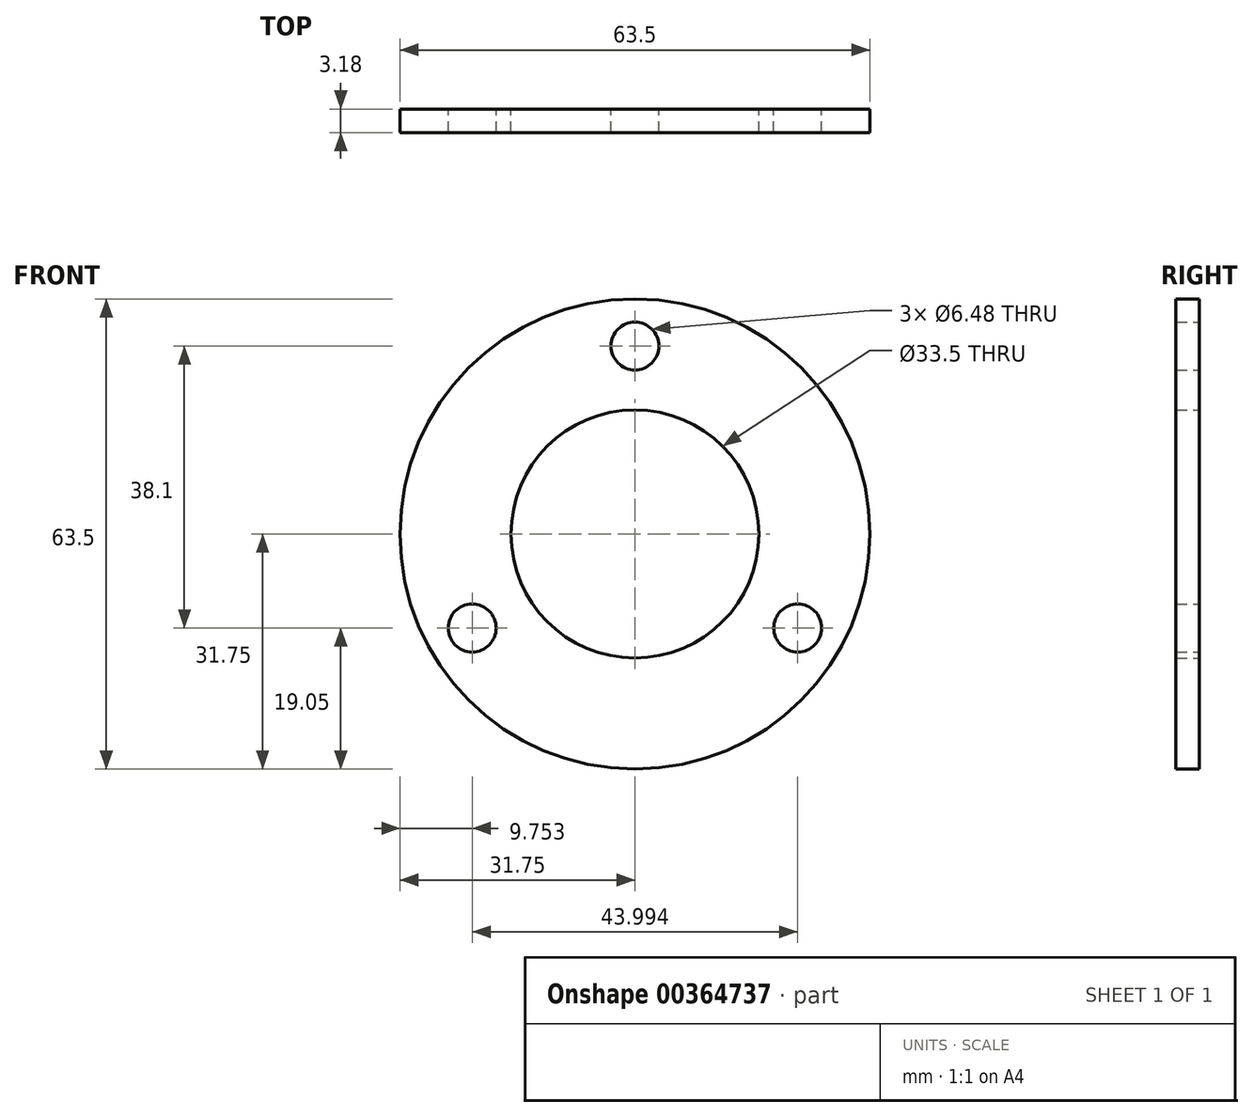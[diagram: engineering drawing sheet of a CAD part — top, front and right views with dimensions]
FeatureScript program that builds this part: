
annotation { "Feature Type Name" : "Feature", "Feature Type Description" : "" }
export const myFeature = defineFeature(function(context is Context, id is Id, definition is map)
    precondition{}
    {
        {
            var Q0;
            Q0=qCreatedBy(makeId("Front.planeOp"),FACE);
            var sketch = newSketch(context, id + "F0", { "sketchPlane" : qUnion([Q0])});
            skCircle(sketch, "E0", {"center": v(0, 0) * mm, "radius": 31.75 * mm});
            skCircle(sketch, "E1", {"center": v(0, 0) * mm, "radius": 16.75 * mm});
            skCircle(sketch, "E2", {"center": v(0, 25.4) * mm, "radius": 3.24 * mm});
            skCircle(sketch, "E3.1.0", {"center": v(-22, -12.7) * mm, "radius": 3.24 * mm});
            skCircle(sketch, "E3.2.0", {"center": v(22, -12.7) * mm, "radius": 3.24 * mm});
            skSolve(sketch);
        }
        {
            var Q0;
            Q0 = qSketchRegion(id + "F0", true);
            extrude(context, id + "F1", {"entities" : qUnion([Q0]), "depth" : 3.17 * mm});
        }
    });
